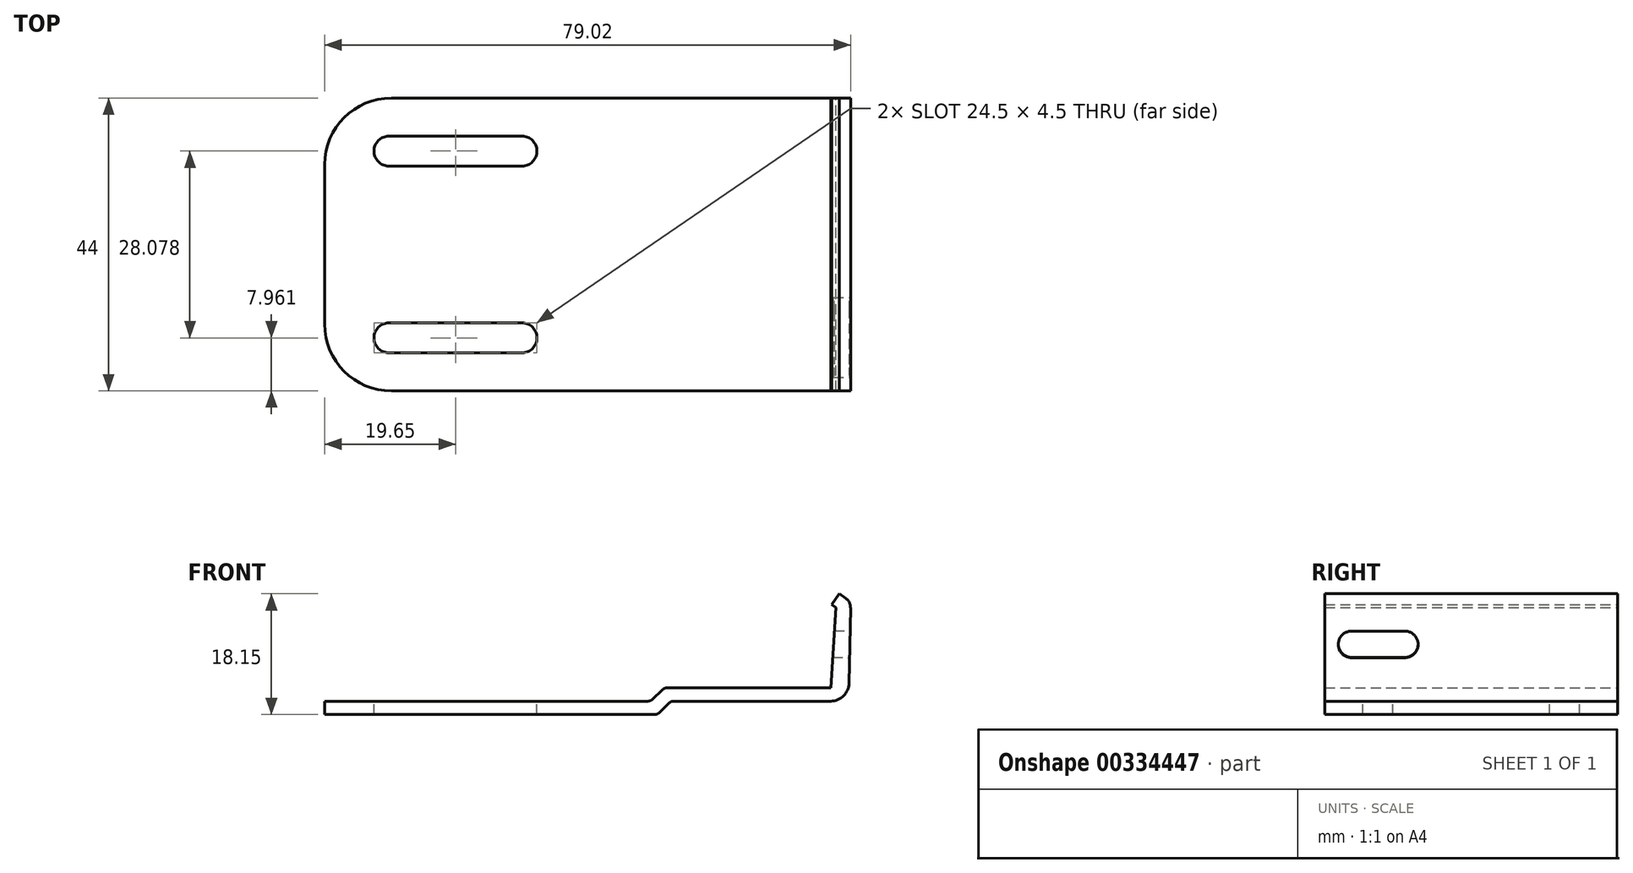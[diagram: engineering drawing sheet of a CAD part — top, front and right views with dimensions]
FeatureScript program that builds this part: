
annotation { "Feature Type Name" : "Feature", "Feature Type Description" : "" }
export const myFeature = defineFeature(function(context is Context, id is Id, definition is map)
    precondition{}
    {
        {
            var Q0;
            Q0=qCreatedBy(makeId("Front.planeOp"),FACE);
            var sketch = newSketch(context, id + "F0", { "sketchPlane" : qUnion([Q0])});
            skLineSegment(sketch, "E0", {"start": v(-0.4, 0) * mm, "end": v(-40, 0) * mm});
            skLineSegment(sketch, "E1", {"start": v(-40, 0) * mm, "end": v(-40, 2) * mm});
            skLineSegment(sketch, "E2", {"start": v(-40, 2) * mm, "end": v(-1.43, 2) * mm});
            skLineSegment(sketch, "E3", {"start": v(-0.73, 2.28) * mm, "end": v(0.75, 3.72) * mm});
            skLineSegment(sketch, "E4", {"start": v(1.44, 4) * mm, "end": v(26.04, 4) * mm});
            skLineSegment(sketch, "E5", {"start": v(0.3, 0.28) * mm, "end": v(1.77, 1.72) * mm});
            skLineSegment(sketch, "E6", {"start": v(2.46, 2) * mm, "end": v(26.04, 2) * mm});
            skPoint(sketch, "E7.visualSharp", {"position": v(-1.02, 2) * mm});
            skArc(sketch, "E7.filletArc", {"start": v(-1.43, 2) * mm, "mid": v(-1.05, 2.07) * mm, "end": v(-0.73, 2.28) * mm});
            skPoint(sketch, "E8.visualSharp", {"position": v(0, 0) * mm});
            skArc(sketch, "E8.filletArc", {"start": v(-0.4, 0) * mm, "mid": v(-0.03, 0.07) * mm, "end": v(0.3, 0.28) * mm});
            skPoint(sketch, "E9.visualSharp", {"position": v(2.06, 2) * mm});
            skArc(sketch, "E9.filletArc", {"start": v(2.46, 2) * mm, "mid": v(2.09, 1.93) * mm, "end": v(1.77, 1.72) * mm});
            skPoint(sketch, "E10.visualSharp", {"position": v(1.04, 4) * mm});
            skArc(sketch, "E10.filletArc", {"start": v(1.44, 4) * mm, "mid": v(1.07, 3.93) * mm, "end": v(0.75, 3.72) * mm});
            skLineSegment(sketch, "E11", {"start": v(26.04, 4) * mm, "end": v(26.83, 16.07) * mm});
            skLineSegment(sketch, "E12", {"start": v(26.83, 16.07) * mm, "end": v(26.19, 16.51) * mm});
            skLineSegment(sketch, "E13", {"start": v(26.19, 16.51) * mm, "end": v(27.33, 18.15) * mm});
            skLineSegment(sketch, "E14", {"start": v(27.33, 18.15) * mm, "end": v(28.27, 17.5) * mm});
            skArc(sketch, "E15", {"start": v(29.02, 16.03) * mm, "mid": v(28.83, 16.85) * mm, "end": v(28.27, 17.5) * mm});
            skLineSegment(sketch, "E16", {"start": v(29.02, 16.03) * mm, "end": v(28.8, 4.7) * mm});
            skArc(sketch, "E17", {"start": v(26.04, 2) * mm, "mid": v(27.97, 2.79) * mm, "end": v(28.8, 4.7) * mm});
            skSolve(sketch);
        }
        {
            var Q0;
            Q0=makeQuery(id+"F0.imprint","IMPRINT",FACE,{"disambiguationData":[TD([[makeQuery(id+"F0.imprint","IMPRINT",EDGE,{"derivedFrom":sQuery(id+"F0.wireOp",EDGE,"E0")}),-1.0]])]});
            extrude(context, id + "F1", {"entities" : qUnion([Q0]), "depth" : 44 * mm, "symmetric" : true});
        }
        {
            var Q0;
            Q0=makeQuery(id+"F1.opExtrude","SWEPT_FACE",FACE,{"disambiguationData":[OSD([sQuery(id+"F0.wireOp",EDGE,"E2")])]});
            var sketch = newSketch(context, id + "F2", { "sketchPlane" : qUnion([Q0])});
            skLineSegment(sketch, "E18", {"start": v(-50, -12) * mm, "end": v(-50, 12) * mm});
            skArc(sketch, "E19", {"start": v(-50, -12) * mm, "mid": v(-47.07, -19.07) * mm, "end": v(-40, -22) * mm});
            skArc(sketch, "E20", {"start": v(-50, 12) * mm, "mid": v(-47.07, 19.07) * mm, "end": v(-40, 22) * mm});
            skSolve(sketch);
        }
        {
            var Q0;
            Q0=makeQuery(id+"F2.imprint","IMPRINT",FACE,{"disambiguationData":[TD([[makeQuery(id+"F2.imprint","IMPRINT",EDGE,{"derivedFrom":sQuery(id+"F2.wireOp",EDGE,"E18")}),-1.0]])]});
            extrude(context, id + "F3", {"entities" : qUnion([Q0]), "operationType" : NewBodyOperationType.ADD, "oppositeDirection" : true, "depth" : 2 * mm});
        }
        {
            var Q0;
            {var subQ0=sQuery(id+"F0.wireOp",EDGE,"E2");Q0=makeQuery(id+"F3.boolean.opBoolean","MERGE",FACE,{"derivedFrom":[makeQuery(id+"F1.opExtrude","SWEPT_FACE",FACE,{"disambiguationData":[OSD([subQ0])]}),makeQuery(id+"F3.opExtrude","CAP_FACE",FACE,{"disambiguationData":[OSD([sQuery(id+"F0.wireOp",EDGE,"E1"),subQ0,sQuery(id+"F2.wireOp",EDGE,"E18"),sQuery(id+"F2.wireOp",EDGE,"E19"),sQuery(id+"F2.wireOp",EDGE,"E20")])],"isStart":true})]});}
            var sketch = newSketch(context, id + "F4", { "sketchPlane" : qUnion([Q0])});
            skLineSegment(sketch, "E21.bottom", {"start": v(-40.35, 11.79) * mm, "end": v(-20.35, 11.79) * mm});
            skLineSegment(sketch, "E21.top", {"start": v(-40.35, 16.29) * mm, "end": v(-20.35, 16.29) * mm});
            skArc(sketch, "E22", {"start": v(-40.35, 16.29) * mm, "mid": v(-42.6, 14.04) * mm, "end": v(-40.35, 11.79) * mm});
            skArc(sketch, "E23", {"start": v(-20.35, 11.79) * mm, "mid": v(-18.1, 14.04) * mm, "end": v(-20.35, 16.29) * mm});
            skLineSegment(sketch, "E24.MirrorCS", {"start": v(-40.35, -16.29) * mm, "end": v(-20.35, -16.29) * mm});
            skArc(sketch, "E25.MirrorCS", {"start": v(-20.35, -11.79) * mm, "mid": v(-18.1, -14.04) * mm, "end": v(-20.35, -16.29) * mm});
            skLineSegment(sketch, "E26.MirrorCS", {"start": v(-40.35, -11.79) * mm, "end": v(-20.35, -11.79) * mm});
            skArc(sketch, "E27.MirrorCS", {"start": v(-40.35, -16.29) * mm, "mid": v(-42.6, -14.04) * mm, "end": v(-40.35, -11.79) * mm});
            skSolve(sketch);
        }
        {
            var Q0;
            Q0=makeQuery(id+"F4.imprint","IMPRINT",FACE,{"disambiguationData":[TD([[makeQuery(id+"F4.imprint","IMPRINT",EDGE,{"derivedFrom":sQuery(id+"F4.wireOp",EDGE,"E24.MirrorCS")}),1.0]])]});
            var Q1;
            Q1=makeQuery(id+"F4.imprint","IMPRINT",FACE,{"disambiguationData":[TD([[makeQuery(id+"F4.imprint","IMPRINT",EDGE,{"derivedFrom":sQuery(id+"F4.wireOp",EDGE,"E21.bottom")}),1.0]])]});
            extrude(context, id + "F5", {"entities" : qUnion([Q0, Q1]), "operationType" : NewBodyOperationType.REMOVE, "oppositeDirection" : true, "depth" : 25 * mm});
        }
        {
            var Q0;
            Q0=makeQuery(id+"F1.opExtrude","SWEPT_FACE",FACE,{"disambiguationData":[OSD([sQuery(id+"F0.wireOp",EDGE,"E16")])]});
            var sketch = newSketch(context, id + "F6", { "sketchPlane" : qUnion([Q0])});
            skLineSegment(sketch, "E28.bottom", {"start": v(-18, 13.1) * mm, "end": v(-10, 13.1) * mm});
            skLineSegment(sketch, "E28.top", {"start": v(-18, 9.1) * mm, "end": v(-10, 9.1) * mm});
            skArc(sketch, "E29", {"start": v(-10, 9.1) * mm, "mid": v(-8, 11.1) * mm, "end": v(-10, 13.1) * mm});
            skArc(sketch, "E30", {"start": v(-18, 13.1) * mm, "mid": v(-20, 11.1) * mm, "end": v(-18, 9.1) * mm});
            skSolve(sketch);
        }
        {
            var Q0;
            Q0=makeQuery(id+"F6.imprint","IMPRINT",FACE,{"disambiguationData":[TD([[makeQuery(id+"F6.imprint","IMPRINT",EDGE,{"derivedFrom":sQuery(id+"F6.wireOp",EDGE,"E28.bottom")}),-1.0]])]});
            extrude(context, id + "F7", {"entities" : qUnion([Q0]), "operationType" : NewBodyOperationType.REMOVE, "oppositeDirection" : true, "depth" : 25 * mm});
        }
    });
